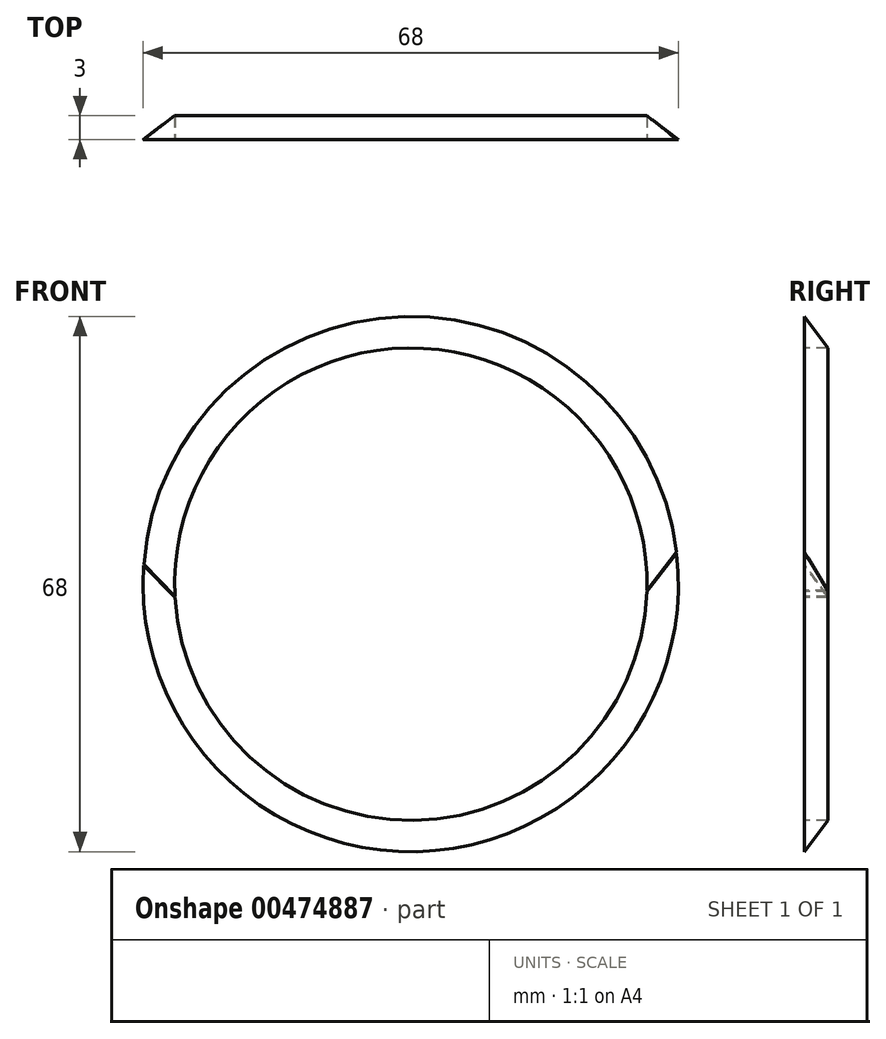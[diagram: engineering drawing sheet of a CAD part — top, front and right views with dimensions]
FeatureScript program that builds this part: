
annotation { "Feature Type Name" : "Feature", "Feature Type Description" : "" }
export const myFeature = defineFeature(function(context is Context, id is Id, definition is map)
    precondition{}
    {
        {
            var Q0;
            Q0=qCreatedBy(makeId("Top.planeOp"),FACE);
            var sketch = newSketch(context, id + "F0", { "sketchPlane" : qUnion([Q0])});
            skLineSegment(sketch, "E0", {"start": v(-39.3, 1.13) * mm, "end": v(-35.3, 1.13) * mm});
            skLineSegment(sketch, "E1", {"start": v(-35.3, 1.13) * mm, "end": v(-35.3, 4.13) * mm});
            skLineSegment(sketch, "E2", {"start": v(-35.3, 4.13) * mm, "end": v(-39.3, 1.13) * mm});
            skLineSegment(sketch, "E3", {"start": v(-5.3, -7.28) * mm, "end": v(-5.3, 15.07) * mm});
            skSolve(sketch);
        }
        {
            var Q0;
            Q0 = qSketchRegion(id + "F0", true);
            var Q1;
            Q1=sQuery(id+"F0.wireOp",EDGE,"E3");
            revolve(context, id + "F1", {"entities" : qUnion([Q0]), "axis" : qUnion([Q1]), "revolveType" : RevolveType.FULL});
        }
        {
            var Q0;
            Q0=qCreatedBy(makeId("Front.planeOp"),FACE);
            var sketch = newSketch(context, id + "F2", { "sketchPlane" : qUnion([Q0])});
            skLineSegment(sketch, "E4", {"start": v(-33.72, -3.26) * mm, "end": v(-41.93, 5.12) * mm});
            skLineSegment(sketch, "E5", {"start": v(23.3, -2.6) * mm, "end": v(31.84, 8.4) * mm});
            skLineSegment(sketch, "E6.0", {"start": v(-33.65, -3.19) * mm, "end": v(-41.86, 5.2) * mm});
            skLineSegment(sketch, "E7", {"start": v(-33.72, -3.26) * mm, "end": v(-33.65, -3.19) * mm});
            skLineSegment(sketch, "E8", {"start": v(-41.93, 5.12) * mm, "end": v(-41.86, 5.2) * mm});
            skLineSegment(sketch, "E9.0", {"start": v(23.37, -2.66) * mm, "end": v(31.92, 8.35) * mm});
            skLineSegment(sketch, "E10", {"start": v(23.3, -2.6) * mm, "end": v(23.37, -2.66) * mm});
            skLineSegment(sketch, "E11", {"start": v(31.84, 8.4) * mm, "end": v(31.92, 8.35) * mm});
            skSolve(sketch);
        }
        {
            var Q0;
            Q0 = qSketchRegion(id + "F2", true);
            extrude(context, id + "F3", {"entities" : qUnion([Q0]), "operationType" : NewBodyOperationType.REMOVE, "endBound" : BoundingType.THROUGH_ALL, "oppositeDirection" : true, "depth" : 25 * mm});
        }
        {
            var Q0;
            Q0=makeQuery(id+"F3.boolean.opBoolean","SPLIT",BODY,{"disambiguationData":[OD(0.0)],"derivedFrom":makeQuery(id+"F1.opRevolve","SWEPT_BODY",BODY,{"disambiguationData":[OSD([sQuery(id+"F0.wireOp",EDGE,"E0"),sQuery(id+"F0.wireOp",EDGE,"E1"),sQuery(id+"F0.wireOp",EDGE,"E2")])]})});
            transform(context, id + "F4", {"entities" : qUnion([Q0]), "transformType" : TransformType.TRANSLATION_3D, "dx" : 0 * mm, "dy" : 0 * mm, "dz" : -3.8 * mm, "makeCopy" : false});
        }
    });
